# Revit family: Fountain-Murdock-A132.8-VR_Series
name_source: partatom
category: Plumbing Fixtures
units: mm (PartAtom-declared; Revit-internal decimal feet)

## family parameters
Cut with Voids When Loaded = No
Host = Face
OmniClass Number = 23.65.70.14.11
OmniClass Title = Drinking Fountains/Coolers
Part Type = Normal
Room Calculation Point = No
Round Connector Dimension = Use Diameter
Shared = Yes

## types (6) — shared parameters
220V - 220 volt / 50 Hz compressor = No
ADA Compliant = Yes
Assembly Code = D2010810
CW Connection = Yes
CWFU = 1.5
Connection Size = 1 1/4"
Default Elevation = 33"
Depth = 18 1/2"
Description = Oval, Chilled Barrier-Free, Bi-Level Wall Mount Drinking Fountain - Sensor Activated
Flow Rate = 8.0  GPH
Full Load Amps = 4.6
HP - High polished stainless steel = No
HW Connection = No
IAPMO Compliance = Unit is certified to ANSI A117.1, Public Law 111-380 (NO-LEAD), CHSC 116875 and NSF/ANSI 61, Section 9. Fixture meets ADA, ADA Standing Person, and ADA Child requirements when mounted appropriately.
Inlet Diameter Connection = 3/8"
Left Height = 41 3/8"
Length = 32 1/4"
Manufacturer = Murdock Manufacturing
Product Documentation Link = https://www.murdockmfg.com
Product Page URL = https://www.murdockmfg.com
RBL - Reverse bi-level = No
Rated Watts = 390
Right Height = 33"
SK4-18 - Skirt kit, stainless steel for upper unit = No
Shipping Weight = 130 Lbs.
URL = https://www.murdockmfg.com
Vent Connection = No
WF1 - 1500 gallon capacity, NSF 42+53, 1 micron lead reduction filter = No
WF3 - 3000 gallon capacity, NSF 42+53, 1 micron lead reduction filter = No
WFU = 2
Waste Connection = Yes
Water Pressure = pressure range of 20-105 psig
Width = 32"
cUPC Compliant = Yes
zero-valued in all types: HWFU

## per-type parameters (varying)
| type | 2 - Bronze finish | 3 - Gold finish (high polished only) | 4 - Stainless Steel (Std) | F - Flexible bubbler | Finish | Material | S - Lead-Free Stainless Steel |
| A132308F-VR | No | Yes | No | Yes | Metal-Murdock-18 Gage-Type 304-Gold | Metal-Murdock-18 Gage-Type 304-Gold | No |
| A132208F-VR | Yes | No | No | Yes | Metal-Murdock-18 Gage-Type 304-Bronze | Metal-Murdock-18 Gage-Type 304-Bronze | No |
| A132408F-VR | No | No | Yes | Yes | Metal-Murdock-18 Gage-Type 304-Stainless Satin | Metal-Murdock-18 Gage-Type 304-Stainless Satin | No |
| A132208S-VR | Yes | No | No | No | Metal-Murdock-18 Gage-Type 304-Bronze | Metal-Murdock-18 Gage-Type 304-Bronze | Yes |
| A132308S-VR | No | Yes | No | No | Metal-Murdock-18 Gage-Type 304-Gold | Metal-Murdock-18 Gage-Type 304-Gold | Yes |
| A132408S-VR | No | No | Yes | No | Metal-Murdock-18 Gage-Type 304-Stainless Satin | Metal-Murdock-18 Gage-Type 304-Stainless Satin | Yes |

note: column(s) folded — value = type name in every type: Model

## geometry (parser evidence)
native form markers: Sweep x3
no freeform markers — native parametric forms only
